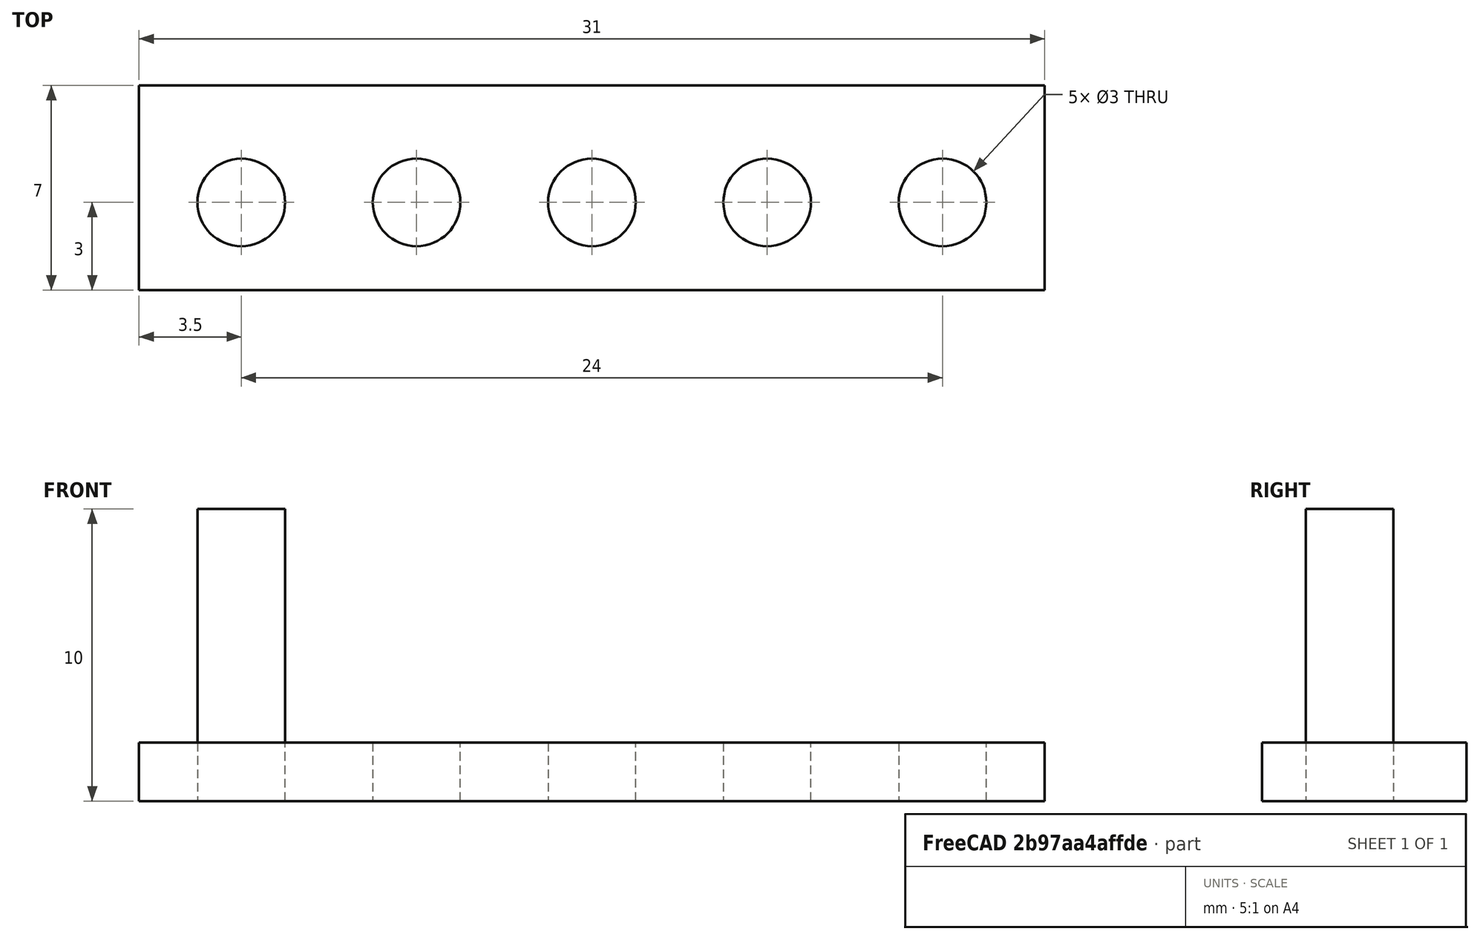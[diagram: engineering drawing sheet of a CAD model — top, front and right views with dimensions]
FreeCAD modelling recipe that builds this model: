
FCSTD DOCUMENT  (FreeCAD 1.0R39319 (Git))
Label: ojt1_t10r01_array_cilinder
License: All rights reserved
LicenseURL: https://en.wikipedia.org/wiki/All_rights_reserved
objects: PartDesign::Body×1, Part::Cylinder×1, Part::FeaturePython×1, Part::Box×1, Part::Cut×1
note: 4 computed .brp shape members not serialized (recipe doc carries the construction recipe); baked Part::Feature solids carry a one-line shape summary decoded from their .brp

FEATURE [PartDesign::Body] Body  label="Cos"
  AllowCompound = false
  Origin = -> Origin
FEATURE [Part::Cylinder] Cylinder  label="Cilindre"
  Angle = 360
  AttacherType = Attacher::AttachEngine3D
  FirstAngle = 0
  Height = 10
  Radius = 1.5
  SecondAngle = 0
FEATURE [Part::FeaturePython] Array  # Draft array (typed FeaturePython)
  AlwaysSyncPlacement = false
  Angle = 360
  ArrayType = 0
  Axis = (0,0,1)
  Base = -> Cylinder
  Center = (0,0,0)
  Count = 5
  ExpandArray = false
  Fuse = false
  IntervalAxis = (0,0,0)
  IntervalX = (6,0,0)
  IntervalY = (0,0,0)
  IntervalZ = (0,0,100)
  NumberCircles = 3
  NumberPolar = 5
  NumberX = 5
  NumberY = 1
  NumberZ = 1
  Placement = pos=(0,0,-1) rot=(0,0,1;0rad)
  PlacementList = 5 placements: arithmetic series from (0,0,0) step (6,0,0) to (24,0,0)
  RadialDistance = 50
  ScaleList = (5) [(1,1,1),(1,1,1),(1,1,1),(1,1,1),(1,1,1)]
  Symmetry = 1
  TangentialDistance = 25
FEATURE [Part::Box] Box  label="Cub"
  AttacherType = Attacher::AttachEngine3D
  Height = 2
  Length = 31
  Placement = pos=(-3.5,-3,0) rot=(0,0,1;0rad)
  Width = 7
FEATURE [Part::Cut] Cut
  Base = -> Box
  Tool = -> Array
